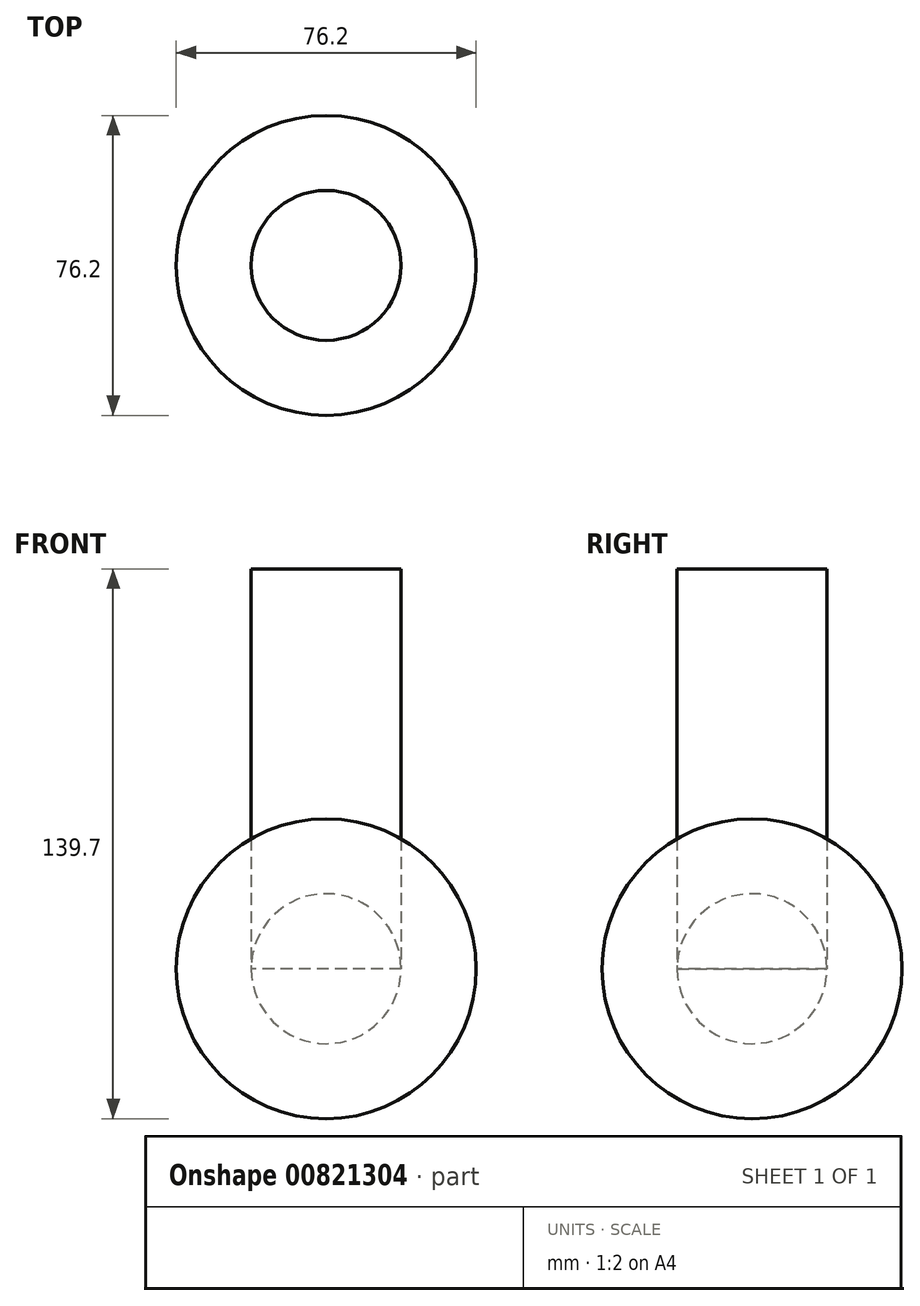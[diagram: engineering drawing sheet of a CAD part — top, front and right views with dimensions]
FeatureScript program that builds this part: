
annotation { "Feature Type Name" : "Feature", "Feature Type Description" : "" }
export const myFeature = defineFeature(function(context is Context, id is Id, definition is map)
    precondition{}
    {
        {
            var Q0;
            Q0=qCreatedBy(makeId("Top.planeOp"),FACE);
            var sketch = newSketch(context, id + "F0", { "sketchPlane" : qUnion([Q0])});
            skCircle(sketch, "E0", {"center": v(0, 0) * mm, "radius": 38.1 * mm});
            skLineSegment(sketch, "E1", {"start": v(0, 0) * mm, "end": v(0, 38.1) * mm});
            skLineSegment(sketch, "E2", {"start": v(0, 0) * mm, "end": v(0, -38.1) * mm});
            skCircle(sketch, "E3", {"center": v(0, 0) * mm, "radius": 19.05 * mm});
            skSolve(sketch);
        }
        {
            var Q0;
            {var subQ0=sQuery(id+"F0.wireOp",EDGE,"E1");var subQ1=sQuery(id+"F0.wireOp",EDGE,"E0");var subQ2=makeQuery(id+"F0.imprint","INTERSECT",VERTEX,{"derivedFrom":[subQ1,subQ0]});Q0=makeQuery(id+"F0.imprint","IMPRINT",FACE,{"disambiguationData":[TD([[makeQuery(id+"F0.imprint","IMPRINT",EDGE,{"disambiguationData":[TD([[subQ2,-1.0]])],"derivedFrom":subQ1}),1.0]])]});}
            var Q1;
            Q1=sQuery(id+"F0.wireOp",EDGE,"E1");
            revolve(context, id + "F1", {"surfaceOperationType" : NewSurfaceOperationType.NEW, "entities" : qUnion([Q0]), "axis" : qUnion([Q1]), "revolveType" : RevolveType.FULL});
        }
        {
            var Q0;
            {var subQ0=sQuery(id+"F0.wireOp",EDGE,"E2");var subQ1=sQuery(id+"F0.wireOp",EDGE,"E1");var subQ2=makeQuery(id+"F0.imprint","INTERSECT",VERTEX,{"derivedFrom":[subQ1,subQ0]});Q0=makeQuery(id+"F0.imprint","IMPRINT",FACE,{"disambiguationData":[TD([[makeQuery(id+"F0.imprint","IMPRINT",EDGE,{"disambiguationData":[TD([[subQ2,-1.0]])],"derivedFrom":subQ1}),1.0]])]});}
            var Q1;
            {var subQ0=sQuery(id+"F0.wireOp",EDGE,"E2");var subQ1=sQuery(id+"F0.wireOp",EDGE,"E1");var subQ2=makeQuery(id+"F0.imprint","INTERSECT",VERTEX,{"derivedFrom":[subQ1,subQ0]});Q1=makeQuery(id+"F0.imprint","IMPRINT",FACE,{"disambiguationData":[TD([[makeQuery(id+"F0.imprint","IMPRINT",EDGE,{"disambiguationData":[TD([[subQ2,-1.0]])],"derivedFrom":subQ1}),-1.0]])]});}
            extrude(context, id + "F2", {"entities" : qUnion([Q0, Q1]), "depth" : 101.6 * mm, "offsetDistance" : 25.4 * mm});
        }
    });
